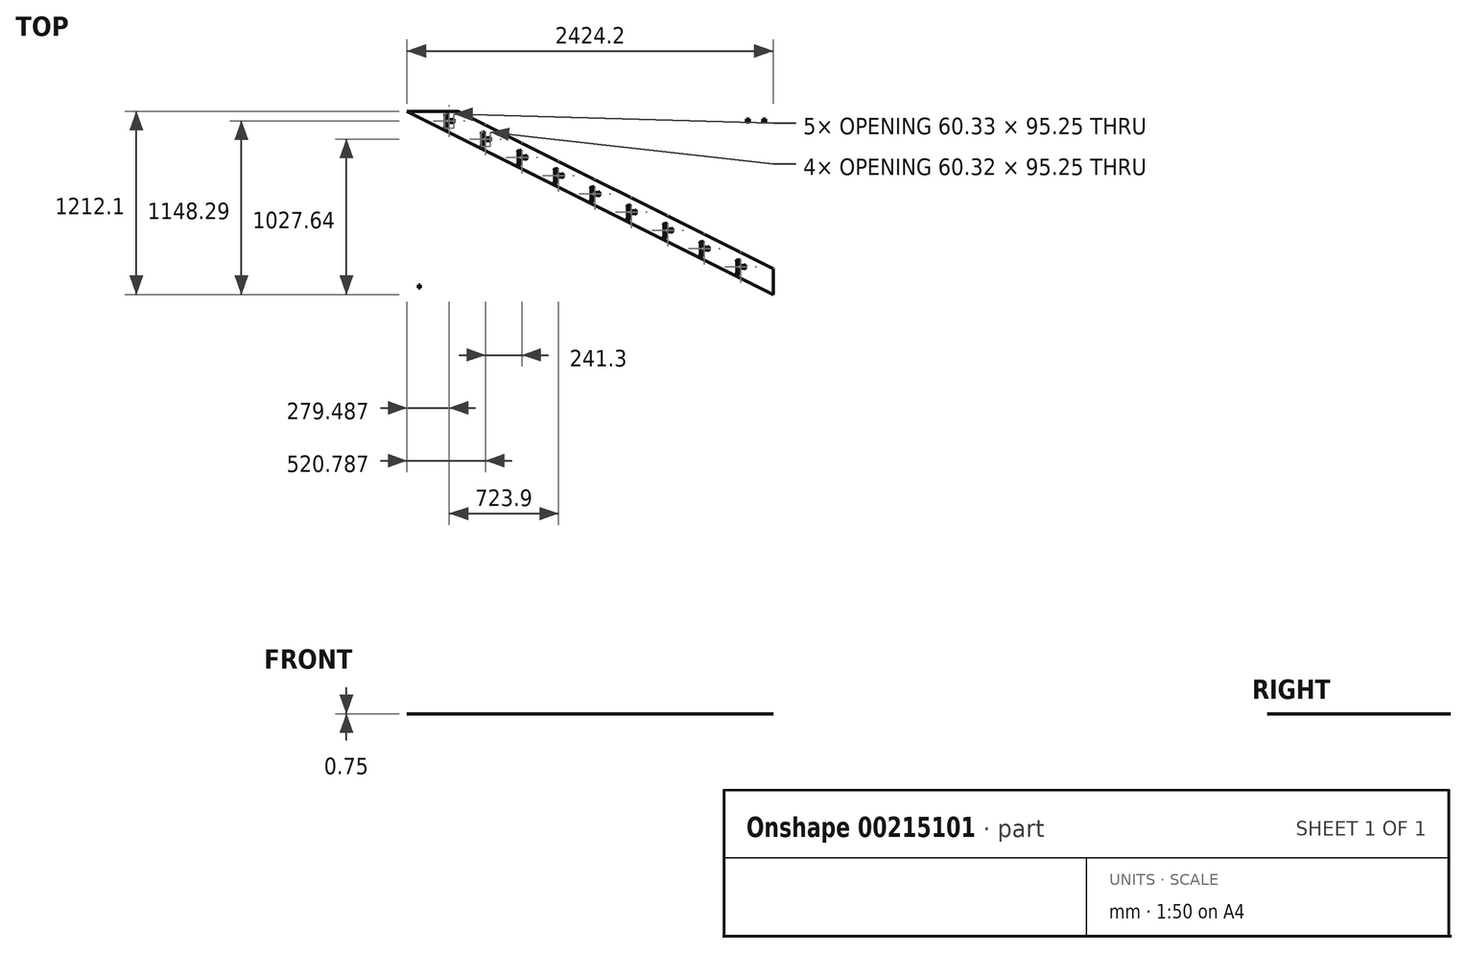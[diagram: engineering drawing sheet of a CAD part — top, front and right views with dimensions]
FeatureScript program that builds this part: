
annotation { "Feature Type Name" : "Feature", "Feature Type Description" : "" }
export const myFeature = defineFeature(function(context is Context, id is Id, definition is map)
    precondition{}
    {
        {
            assignVariable(context, id + "F0", {"name" : "Thickness", "anyValue" : 0.75});
        }
        {
            var Q0;
            Q0=qCreatedBy(makeId("Top.planeOp"),FACE);
            var sketch = newSketch(context, id + "F1", { "sketchPlane" : qUnion([Q0])});
            skLineSegment(sketch, "E0.0.0", {"start": v(-1223, -613.4) * mm, "end": v(1215.4, -613.4) * mm});
            skLineSegment(sketch, "E0.0.1", {"start": v(1215.4, -613.4) * mm, "end": v(1215.4, 605.8) * mm});
            skLineSegment(sketch, "E0.0.2", {"start": v(1215.4, 605.8) * mm, "end": v(-1223, 605.8) * mm});
            skLineSegment(sketch, "E0.0.3", {"start": v(-1223, 605.8) * mm, "end": v(-1223, -613.4) * mm});
            skLineSegment(sketch, "E1", {"start": v(-1223, 605.8) * mm, "end": v(1215.4, -613.4) * mm, "construction": true});
            skLineSegment(sketch, "E2.0", {"start": v(-1208.81, 605.8) * mm, "end": v(1215.4, -606.31) * mm});
            skLineSegment(sketch, "E3.0", {"start": v(-868.03, 605.8) * mm, "end": v(1215.4, -435.92) * mm});
            skLineSegment(sketch, "E4.1.0.0", {"start": v(974.1, -613.41) * mm, "end": v(974.1, 605.8) * mm, "construction": true});
            skLineSegment(sketch, "E4.2.0.0", {"start": v(732.8, -613.4) * mm, "end": v(732.8, 605.8) * mm, "construction": true});
            skLineSegment(sketch, "E4.direction1", {"start": v(1215.4, -613.4) * mm, "end": v(974.1, -613.4) * mm, "construction": true});
            skLineSegment(sketch, "E5.0.3.0", {"start": v(491.5, -613.4) * mm, "end": v(491.5, 605.8) * mm, "construction": true});
            skLineSegment(sketch, "E5.0.4.0", {"start": v(250.2, -613.4) * mm, "end": v(250.2, 605.8) * mm, "construction": true});
            skLineSegment(sketch, "E5.0.5.0", {"start": v(8.9, -613.4) * mm, "end": v(8.9, 605.8) * mm, "construction": true});
            skLineSegment(sketch, "E5.0.6.0", {"start": v(-232.4, -613.4) * mm, "end": v(-232.4, 605.8) * mm, "construction": true});
            skLineSegment(sketch, "E5.0.7.0", {"start": v(-473.7, -613.4) * mm, "end": v(-473.7, 605.8) * mm, "construction": true});
            skLineSegment(sketch, "E5.0.8.0", {"start": v(-715, -613.4) * mm, "end": v(-715, 605.8) * mm, "construction": true});
            skLineSegment(sketch, "E6.0.9.0", {"start": v(-956.3, -613.4) * mm, "end": v(-956.3, 605.8) * mm, "construction": true});
            skLineSegment(sketch, "E7.0.10.0", {"start": v(-1197.6, -613.4) * mm, "end": v(-1197.6, 605.8) * mm, "construction": true});
            skLineSegment(sketch, "E8.bottom", {"start": v(-956.31, 586.43) * mm, "end": v(-937.26, 586.43) * mm});
            skLineSegment(sketch, "E8.top", {"start": v(-956.31, 497.53) * mm, "end": v(-937.26, 497.53) * mm});
            skLineSegment(sketch, "E8.left", {"start": v(-956.3, 586.43) * mm, "end": v(-956.3, 497.53) * mm});
            skLineSegment(sketch, "E8.right", {"start": v(-937.26, 586.43) * mm, "end": v(-937.26, 497.53) * mm});
            skLineSegment(sketch, "E9.bottom", {"start": v(-715.01, 465.78) * mm, "end": v(-695.96, 465.78) * mm});
            skLineSegment(sketch, "E9.top", {"start": v(-715.01, 376.88) * mm, "end": v(-695.96, 376.88) * mm});
            skLineSegment(sketch, "E9.left", {"start": v(-715, 465.78) * mm, "end": v(-715, 376.88) * mm});
            skLineSegment(sketch, "E9.right", {"start": v(-695.96, 465.78) * mm, "end": v(-695.96, 376.88) * mm});
            skLineSegment(sketch, "E10.bottom", {"start": v(-473.71, 345.13) * mm, "end": v(-454.66, 345.13) * mm});
            skLineSegment(sketch, "E10.top", {"start": v(-473.7, 256.23) * mm, "end": v(-454.66, 256.23) * mm});
            skLineSegment(sketch, "E10.left", {"start": v(-473.7, 345.13) * mm, "end": v(-473.7, 256.23) * mm});
            skLineSegment(sketch, "E10.right", {"start": v(-454.66, 345.13) * mm, "end": v(-454.66, 256.23) * mm});
            skLineSegment(sketch, "E11.bottom", {"start": v(-232.4, 224.48) * mm, "end": v(-213.36, 224.48) * mm});
            skLineSegment(sketch, "E11.top", {"start": v(-232.4, 135.58) * mm, "end": v(-213.36, 135.58) * mm});
            skLineSegment(sketch, "E11.left", {"start": v(-232.4, 224.48) * mm, "end": v(-232.4, 135.58) * mm});
            skLineSegment(sketch, "E11.right", {"start": v(-213.36, 224.48) * mm, "end": v(-213.36, 135.58) * mm});
            skLineSegment(sketch, "E12.bottom", {"start": v(8.9, 103.83) * mm, "end": v(27.94, 103.83) * mm});
            skLineSegment(sketch, "E12.top", {"start": v(8.9, 14.93) * mm, "end": v(27.94, 14.93) * mm});
            skLineSegment(sketch, "E12.left", {"start": v(8.9, 103.83) * mm, "end": v(8.9, 14.93) * mm});
            skLineSegment(sketch, "E12.right", {"start": v(27.94, 103.83) * mm, "end": v(27.94, 14.93) * mm});
            skLineSegment(sketch, "E13.bottom", {"start": v(250.2, -16.82) * mm, "end": v(269.24, -16.82) * mm});
            skLineSegment(sketch, "E13.top", {"start": v(250.2, -105.72) * mm, "end": v(269.24, -105.72) * mm});
            skLineSegment(sketch, "E13.left", {"start": v(250.2, -16.82) * mm, "end": v(250.2, -105.72) * mm});
            skLineSegment(sketch, "E13.right", {"start": v(269.24, -16.82) * mm, "end": v(269.24, -105.72) * mm});
            skLineSegment(sketch, "E14.bottom", {"start": v(491.5, -137.47) * mm, "end": v(510.54, -137.47) * mm});
            skLineSegment(sketch, "E14.top", {"start": v(491.5, -226.37) * mm, "end": v(510.54, -226.37) * mm});
            skLineSegment(sketch, "E14.left", {"start": v(491.5, -137.47) * mm, "end": v(491.5, -226.37) * mm});
            skLineSegment(sketch, "E14.right", {"start": v(510.54, -137.47) * mm, "end": v(510.54, -226.37) * mm});
            skLineSegment(sketch, "E15.bottom", {"start": v(732.8, -258.12) * mm, "end": v(751.84, -258.12) * mm});
            skLineSegment(sketch, "E15.top", {"start": v(732.8, -347.02) * mm, "end": v(751.84, -347.02) * mm});
            skLineSegment(sketch, "E15.left", {"start": v(732.8, -258.12) * mm, "end": v(732.8, -347.02) * mm});
            skLineSegment(sketch, "E15.right", {"start": v(751.84, -258.12) * mm, "end": v(751.84, -347.02) * mm});
            skLineSegment(sketch, "E16.bottom", {"start": v(974.1, -378.77) * mm, "end": v(993.14, -378.77) * mm});
            skLineSegment(sketch, "E16.top", {"start": v(974.1, -467.67) * mm, "end": v(993.14, -467.67) * mm});
            skLineSegment(sketch, "E16.left", {"start": v(974.1, -378.77) * mm, "end": v(974.1, -467.67) * mm});
            skLineSegment(sketch, "E16.right", {"start": v(993.14, -378.77) * mm, "end": v(993.14, -467.67) * mm});
            skPoint(sketch, "E17", {"position": v(-715.01, 529.28) * mm});
            skPoint(sketch, "E18", {"position": v(-715, 358.89) * mm});
            skPoint(sketch, "E19", {"position": v(-473.71, 408.63) * mm});
            skPoint(sketch, "E20", {"position": v(-956.31, 649.93) * mm});
            skPoint(sketch, "E21", {"position": v(-232.41, 287.98) * mm});
            skPoint(sketch, "E22", {"position": v(8.89, 167.33) * mm});
            skPoint(sketch, "E23", {"position": v(250.19, 46.68) * mm});
            skPoint(sketch, "E24", {"position": v(491.49, -73.97) * mm});
            skPoint(sketch, "E25", {"position": v(732.8, -194.62) * mm});
            skPoint(sketch, "E26", {"position": v(974.1, -315.27) * mm});
            skLineSegment(sketch, "E27.top", {"start": v(-937.26, 532.45) * mm, "end": v(-899.16, 532.45) * mm});
            skLineSegment(sketch, "E27.left", {"start": v(-937.26, 551.5) * mm, "end": v(-937.26, 532.45) * mm});
            skLineSegment(sketch, "E27.right", {"start": v(-899.16, 551.5) * mm, "end": v(-899.16, 532.45) * mm});
            skLineSegment(sketch, "E28.bottom", {"start": v(-695.96, 430.85) * mm, "end": v(-657.86, 430.85) * mm});
            skLineSegment(sketch, "E28.top", {"start": v(-695.96, 411.8) * mm, "end": v(-657.86, 411.8) * mm});
            skLineSegment(sketch, "E28.left", {"start": v(-695.96, 430.85) * mm, "end": v(-695.96, 411.8) * mm});
            skLineSegment(sketch, "E28.right", {"start": v(-657.86, 430.85) * mm, "end": v(-657.86, 411.8) * mm});
            skLineSegment(sketch, "E29.bottom", {"start": v(-454.66, 310.2) * mm, "end": v(-416.56, 310.2) * mm});
            skLineSegment(sketch, "E29.top", {"start": v(-454.66, 291.15) * mm, "end": v(-416.56, 291.15) * mm});
            skLineSegment(sketch, "E29.left", {"start": v(-454.66, 310.2) * mm, "end": v(-454.66, 291.15) * mm});
            skLineSegment(sketch, "E29.right", {"start": v(-416.56, 310.2) * mm, "end": v(-416.56, 291.15) * mm});
            skLineSegment(sketch, "E30.bottom", {"start": v(-213.36, 189.55) * mm, "end": v(-175.26, 189.55) * mm});
            skLineSegment(sketch, "E30.top", {"start": v(-213.36, 170.5) * mm, "end": v(-175.26, 170.5) * mm});
            skLineSegment(sketch, "E30.left", {"start": v(-213.36, 189.55) * mm, "end": v(-213.36, 170.5) * mm});
            skLineSegment(sketch, "E30.right", {"start": v(-175.26, 189.55) * mm, "end": v(-175.26, 170.5) * mm});
            skLineSegment(sketch, "E31.bottom", {"start": v(27.94, 68.9) * mm, "end": v(66.04, 68.9) * mm});
            skLineSegment(sketch, "E31.top", {"start": v(27.94, 49.85) * mm, "end": v(66.04, 49.85) * mm});
            skLineSegment(sketch, "E31.left", {"start": v(27.94, 68.9) * mm, "end": v(27.94, 49.85) * mm});
            skLineSegment(sketch, "E31.right", {"start": v(66.04, 68.9) * mm, "end": v(66.04, 49.85) * mm});
            skPoint(sketch, "E32", {"position": v(-899.16, 541.98) * mm});
            skPoint(sketch, "E33", {"position": v(-657.86, 421.33) * mm});
            skPoint(sketch, "E34", {"position": v(-416.56, 300.68) * mm});
            skPoint(sketch, "E35", {"position": v(-175.26, 180.03) * mm});
            skPoint(sketch, "E36", {"position": v(66.04, 59.38) * mm});
            skLineSegment(sketch, "E37.bottom", {"start": v(269.24, -51.75) * mm, "end": v(307.34, -51.75) * mm});
            skLineSegment(sketch, "E37.top", {"start": v(269.24, -70.8) * mm, "end": v(307.34, -70.8) * mm});
            skLineSegment(sketch, "E37.left", {"start": v(269.24, -51.75) * mm, "end": v(269.24, -70.8) * mm});
            skLineSegment(sketch, "E37.right", {"start": v(307.34, -51.75) * mm, "end": v(307.34, -70.8) * mm});
            skPoint(sketch, "E38", {"position": v(307.34, -61.27) * mm});
            skLineSegment(sketch, "E39.bottom", {"start": v(510.54, -172.4) * mm, "end": v(548.64, -172.4) * mm});
            skLineSegment(sketch, "E39.top", {"start": v(510.54, -191.45) * mm, "end": v(548.64, -191.45) * mm});
            skLineSegment(sketch, "E39.left", {"start": v(510.54, -172.4) * mm, "end": v(510.54, -191.45) * mm});
            skLineSegment(sketch, "E39.right", {"start": v(548.64, -172.4) * mm, "end": v(548.64, -191.45) * mm});
            skPoint(sketch, "E40", {"position": v(548.64, -181.92) * mm});
            skLineSegment(sketch, "E41.bottom", {"start": v(751.84, -293.05) * mm, "end": v(789.94, -293.05) * mm});
            skLineSegment(sketch, "E41.top", {"start": v(751.84, -312.1) * mm, "end": v(789.94, -312.1) * mm});
            skLineSegment(sketch, "E41.left", {"start": v(751.84, -293.05) * mm, "end": v(751.84, -312.1) * mm});
            skLineSegment(sketch, "E41.right", {"start": v(789.94, -293.05) * mm, "end": v(789.94, -312.1) * mm});
            skLineSegment(sketch, "E42.bottom", {"start": v(993.14, -413.7) * mm, "end": v(1031.24, -413.7) * mm});
            skLineSegment(sketch, "E42.top", {"start": v(993.14, -432.75) * mm, "end": v(1031.24, -432.75) * mm});
            skLineSegment(sketch, "E42.left", {"start": v(993.14, -413.7) * mm, "end": v(993.14, -432.75) * mm});
            skLineSegment(sketch, "E42.right", {"start": v(1031.24, -413.7) * mm, "end": v(1031.24, -432.75) * mm});
            skPoint(sketch, "E43", {"position": v(1031.24, -423.22) * mm});
            skLineSegment(sketch, "E44.bottom", {"start": v(-1172.2, -562.6) * mm, "end": v(-1121.4, -562.6) * mm});
            skLineSegment(sketch, "E44.top", {"start": v(-1172.2, -54.6) * mm, "end": v(-1121.4, -54.6) * mm});
            skLineSegment(sketch, "E44.left", {"start": v(-1172.2, -562.6) * mm, "end": v(-1172.2, -54.6) * mm});
            skLineSegment(sketch, "E44.right", {"start": v(-1121.4, -562.6) * mm, "end": v(-1121.4, -54.61) * mm});
            skLineSegment(sketch, "E45.bottom", {"start": v(-1121.4, -54.6) * mm, "end": v(-1134.1, -54.6) * mm});
            skLineSegment(sketch, "E45.top", {"start": v(-1121.4, -73.66) * mm, "end": v(-1134.1, -73.66) * mm});
            skLineSegment(sketch, "E45.left", {"start": v(-1121.4, -54.61) * mm, "end": v(-1121.4, -73.66) * mm});
            skLineSegment(sketch, "E45.right", {"start": v(-1134.1, -54.61) * mm, "end": v(-1134.1, -73.66) * mm});
            skLineSegment(sketch, "E46.bottom", {"start": v(-1121.4, -562.6) * mm, "end": v(-1134.1, -562.6) * mm});
            skLineSegment(sketch, "E46.top", {"start": v(-1121.4, -543.56) * mm, "end": v(-1134.1, -543.56) * mm});
            skLineSegment(sketch, "E46.left", {"start": v(-1121.4, -562.6) * mm, "end": v(-1121.4, -543.56) * mm});
            skLineSegment(sketch, "E46.right", {"start": v(-1134.1, -562.61) * mm, "end": v(-1134.1, -543.56) * mm});
            skLineSegment(sketch, "E47.1.0.0", {"start": v(-1062.99, -73.66) * mm, "end": v(-1075.69, -73.66) * mm});
            skLineSegment(sketch, "E47.1.0.1", {"start": v(-1075.69, -54.61) * mm, "end": v(-1075.69, -73.66) * mm});
            skLineSegment(sketch, "E47.1.0.2", {"start": v(-1075.69, -562.61) * mm, "end": v(-1075.69, -543.56) * mm});
            skLineSegment(sketch, "E47.1.0.3", {"start": v(-1113.8, -562.6) * mm, "end": v(-1062.99, -562.6) * mm});
            skLineSegment(sketch, "E47.1.0.4", {"start": v(-1113.79, -54.6) * mm, "end": v(-1062.99, -54.6) * mm});
            skLineSegment(sketch, "E47.1.0.5", {"start": v(-1113.8, -562.6) * mm, "end": v(-1113.79, -54.6) * mm});
            skLineSegment(sketch, "E47.1.0.6", {"start": v(-1062.99, -562.6) * mm, "end": v(-1062.99, -54.61) * mm});
            skLineSegment(sketch, "E47.1.0.7", {"start": v(-1062.99, -54.6) * mm, "end": v(-1075.69, -54.6) * mm});
            skLineSegment(sketch, "E47.1.0.8", {"start": v(-1062.99, -54.61) * mm, "end": v(-1062.99, -73.66) * mm});
            skLineSegment(sketch, "E47.1.0.9", {"start": v(-1062.99, -562.6) * mm, "end": v(-1062.99, -543.56) * mm});
            skLineSegment(sketch, "E47.1.0.10", {"start": v(-1062.99, -562.6) * mm, "end": v(-1075.69, -562.6) * mm});
            skLineSegment(sketch, "E47.1.0.11", {"start": v(-1062.99, -543.56) * mm, "end": v(-1075.7, -543.56) * mm});
            skLineSegment(sketch, "E47.2.0.0", {"start": v(-1004.57, -73.66) * mm, "end": v(-1017.27, -73.66) * mm});
            skLineSegment(sketch, "E47.2.0.1", {"start": v(-1017.27, -54.61) * mm, "end": v(-1017.27, -73.66) * mm});
            skLineSegment(sketch, "E47.2.0.2", {"start": v(-1017.27, -562.61) * mm, "end": v(-1017.27, -543.56) * mm});
            skLineSegment(sketch, "E47.2.0.3", {"start": v(-1055.37, -562.6) * mm, "end": v(-1004.57, -562.6) * mm});
            skLineSegment(sketch, "E47.2.0.4", {"start": v(-1055.37, -54.6) * mm, "end": v(-1004.57, -54.6) * mm});
            skLineSegment(sketch, "E47.2.0.5", {"start": v(-1055.37, -562.6) * mm, "end": v(-1055.37, -54.6) * mm});
            skLineSegment(sketch, "E47.2.0.6", {"start": v(-1004.57, -562.6) * mm, "end": v(-1004.57, -54.61) * mm});
            skLineSegment(sketch, "E47.2.0.7", {"start": v(-1004.57, -54.6) * mm, "end": v(-1017.27, -54.6) * mm});
            skLineSegment(sketch, "E47.2.0.8", {"start": v(-1004.57, -54.61) * mm, "end": v(-1004.57, -73.66) * mm});
            skLineSegment(sketch, "E47.2.0.9", {"start": v(-1004.57, -562.6) * mm, "end": v(-1004.57, -543.56) * mm});
            skLineSegment(sketch, "E47.2.0.10", {"start": v(-1004.57, -562.6) * mm, "end": v(-1017.27, -562.6) * mm});
            skLineSegment(sketch, "E47.2.0.11", {"start": v(-1004.57, -543.56) * mm, "end": v(-1017.27, -543.56) * mm});
            skLineSegment(sketch, "E47.3.0.0", {"start": v(-946.15, -73.66) * mm, "end": v(-958.85, -73.66) * mm});
            skLineSegment(sketch, "E47.3.0.1", {"start": v(-958.85, -54.61) * mm, "end": v(-958.85, -73.66) * mm});
            skLineSegment(sketch, "E47.3.0.2", {"start": v(-958.85, -562.61) * mm, "end": v(-958.85, -543.56) * mm});
            skLineSegment(sketch, "E47.3.0.3", {"start": v(-996.95, -562.6) * mm, "end": v(-946.15, -562.6) * mm});
            skLineSegment(sketch, "E47.3.0.4", {"start": v(-996.95, -54.6) * mm, "end": v(-946.15, -54.6) * mm});
            skLineSegment(sketch, "E47.3.0.5", {"start": v(-996.95, -562.6) * mm, "end": v(-996.95, -54.6) * mm});
            skLineSegment(sketch, "E47.3.0.6", {"start": v(-946.15, -562.6) * mm, "end": v(-946.15, -54.61) * mm});
            skLineSegment(sketch, "E47.3.0.7", {"start": v(-946.15, -54.6) * mm, "end": v(-958.85, -54.6) * mm});
            skLineSegment(sketch, "E47.3.0.8", {"start": v(-946.15, -54.61) * mm, "end": v(-946.15, -73.66) * mm});
            skLineSegment(sketch, "E47.3.0.9", {"start": v(-946.15, -562.6) * mm, "end": v(-946.15, -543.56) * mm});
            skLineSegment(sketch, "E47.3.0.10", {"start": v(-946.15, -562.6) * mm, "end": v(-958.85, -562.6) * mm});
            skLineSegment(sketch, "E47.3.0.11", {"start": v(-946.15, -543.56) * mm, "end": v(-958.85, -543.56) * mm});
            skLineSegment(sketch, "E47.4.0.0", {"start": v(-887.73, -73.66) * mm, "end": v(-900.43, -73.66) * mm});
            skLineSegment(sketch, "E47.4.0.1", {"start": v(-900.43, -54.61) * mm, "end": v(-900.43, -73.66) * mm});
            skLineSegment(sketch, "E47.4.0.2", {"start": v(-900.43, -562.61) * mm, "end": v(-900.43, -543.56) * mm});
            skLineSegment(sketch, "E47.4.0.3", {"start": v(-938.53, -562.6) * mm, "end": v(-887.73, -562.6) * mm});
            skLineSegment(sketch, "E47.4.0.4", {"start": v(-938.53, -54.6) * mm, "end": v(-887.73, -54.6) * mm});
            skLineSegment(sketch, "E47.4.0.5", {"start": v(-938.53, -562.6) * mm, "end": v(-938.53, -54.6) * mm});
            skLineSegment(sketch, "E47.4.0.6", {"start": v(-887.73, -562.6) * mm, "end": v(-887.73, -54.61) * mm});
            skLineSegment(sketch, "E47.4.0.7", {"start": v(-887.73, -54.6) * mm, "end": v(-900.43, -54.6) * mm});
            skLineSegment(sketch, "E47.4.0.8", {"start": v(-887.73, -54.61) * mm, "end": v(-887.73, -73.66) * mm});
            skLineSegment(sketch, "E47.4.0.9", {"start": v(-887.73, -562.6) * mm, "end": v(-887.73, -543.56) * mm});
            skLineSegment(sketch, "E47.4.0.10", {"start": v(-887.73, -562.6) * mm, "end": v(-900.43, -562.6) * mm});
            skLineSegment(sketch, "E47.4.0.11", {"start": v(-887.73, -543.56) * mm, "end": v(-900.43, -543.56) * mm});
            skLineSegment(sketch, "E47.5.0.0", {"start": v(-829.31, -73.66) * mm, "end": v(-842.01, -73.66) * mm});
            skLineSegment(sketch, "E47.5.0.1", {"start": v(-842.01, -54.61) * mm, "end": v(-842.01, -73.66) * mm});
            skLineSegment(sketch, "E47.5.0.2", {"start": v(-842.01, -562.61) * mm, "end": v(-842.01, -543.56) * mm});
            skLineSegment(sketch, "E47.5.0.3", {"start": v(-880.11, -562.6) * mm, "end": v(-829.31, -562.6) * mm});
            skLineSegment(sketch, "E47.5.0.4", {"start": v(-880.11, -54.6) * mm, "end": v(-829.31, -54.6) * mm});
            skLineSegment(sketch, "E47.5.0.5", {"start": v(-880.11, -562.6) * mm, "end": v(-880.11, -54.6) * mm});
            skLineSegment(sketch, "E47.5.0.6", {"start": v(-829.31, -562.6) * mm, "end": v(-829.31, -54.61) * mm});
            skLineSegment(sketch, "E47.5.0.7", {"start": v(-829.31, -54.6) * mm, "end": v(-842.01, -54.6) * mm});
            skLineSegment(sketch, "E47.5.0.8", {"start": v(-829.31, -54.61) * mm, "end": v(-829.31, -73.66) * mm});
            skLineSegment(sketch, "E47.5.0.9", {"start": v(-829.31, -562.6) * mm, "end": v(-829.31, -543.56) * mm});
            skLineSegment(sketch, "E47.5.0.10", {"start": v(-829.31, -562.6) * mm, "end": v(-842.01, -562.6) * mm});
            skLineSegment(sketch, "E47.5.0.11", {"start": v(-829.31, -543.56) * mm, "end": v(-842.01, -543.56) * mm});
            skLineSegment(sketch, "E47.6.0.0", {"start": v(-770.9, -73.66) * mm, "end": v(-783.6, -73.66) * mm});
            skLineSegment(sketch, "E47.6.0.1", {"start": v(-783.6, -54.61) * mm, "end": v(-783.6, -73.66) * mm});
            skLineSegment(sketch, "E47.6.0.2", {"start": v(-783.6, -562.61) * mm, "end": v(-783.6, -543.56) * mm});
            skLineSegment(sketch, "E47.6.0.3", {"start": v(-821.7, -562.6) * mm, "end": v(-770.9, -562.6) * mm});
            skLineSegment(sketch, "E47.6.0.4", {"start": v(-821.7, -54.6) * mm, "end": v(-770.9, -54.6) * mm});
            skLineSegment(sketch, "E47.6.0.5", {"start": v(-821.7, -562.6) * mm, "end": v(-821.7, -54.6) * mm});
            skLineSegment(sketch, "E47.6.0.6", {"start": v(-770.9, -562.6) * mm, "end": v(-770.9, -54.61) * mm});
            skLineSegment(sketch, "E47.6.0.7", {"start": v(-770.9, -54.6) * mm, "end": v(-783.6, -54.6) * mm});
            skLineSegment(sketch, "E47.6.0.8", {"start": v(-770.9, -54.61) * mm, "end": v(-770.9, -73.66) * mm});
            skLineSegment(sketch, "E47.6.0.9", {"start": v(-770.9, -562.6) * mm, "end": v(-770.9, -543.56) * mm});
            skLineSegment(sketch, "E47.6.0.10", {"start": v(-770.9, -562.6) * mm, "end": v(-783.6, -562.6) * mm});
            skLineSegment(sketch, "E47.6.0.11", {"start": v(-770.9, -543.56) * mm, "end": v(-783.6, -543.56) * mm});
            skLineSegment(sketch, "E47.7.0.0", {"start": v(-712.47, -73.66) * mm, "end": v(-725.17, -73.66) * mm});
            skLineSegment(sketch, "E47.7.0.1", {"start": v(-725.17, -54.61) * mm, "end": v(-725.17, -73.66) * mm});
            skLineSegment(sketch, "E47.7.0.2", {"start": v(-725.17, -562.61) * mm, "end": v(-725.17, -543.56) * mm});
            skLineSegment(sketch, "E47.7.0.3", {"start": v(-763.27, -562.6) * mm, "end": v(-712.47, -562.6) * mm});
            skLineSegment(sketch, "E47.7.0.4", {"start": v(-763.27, -54.6) * mm, "end": v(-712.47, -54.6) * mm});
            skLineSegment(sketch, "E47.7.0.5", {"start": v(-763.27, -562.6) * mm, "end": v(-763.27, -54.6) * mm});
            skLineSegment(sketch, "E47.7.0.6", {"start": v(-712.47, -562.6) * mm, "end": v(-712.47, -54.61) * mm});
            skLineSegment(sketch, "E47.7.0.7", {"start": v(-712.47, -54.6) * mm, "end": v(-725.17, -54.6) * mm});
            skLineSegment(sketch, "E47.7.0.8", {"start": v(-712.47, -54.61) * mm, "end": v(-712.47, -73.66) * mm});
            skLineSegment(sketch, "E47.7.0.9", {"start": v(-712.47, -562.6) * mm, "end": v(-712.47, -543.56) * mm});
            skLineSegment(sketch, "E47.7.0.10", {"start": v(-712.47, -562.6) * mm, "end": v(-725.17, -562.6) * mm});
            skLineSegment(sketch, "E47.7.0.11", {"start": v(-712.47, -543.56) * mm, "end": v(-725.17, -543.56) * mm});
            skLineSegment(sketch, "E47.8.0.0", {"start": v(-654.05, -73.66) * mm, "end": v(-666.75, -73.66) * mm});
            skLineSegment(sketch, "E47.8.0.1", {"start": v(-666.75, -54.61) * mm, "end": v(-666.75, -73.66) * mm});
            skLineSegment(sketch, "E47.8.0.2", {"start": v(-666.75, -562.61) * mm, "end": v(-666.75, -543.56) * mm});
            skLineSegment(sketch, "E47.8.0.3", {"start": v(-704.85, -562.6) * mm, "end": v(-654.05, -562.6) * mm});
            skLineSegment(sketch, "E47.8.0.4", {"start": v(-704.85, -54.6) * mm, "end": v(-654.05, -54.6) * mm});
            skLineSegment(sketch, "E47.8.0.5", {"start": v(-704.85, -562.6) * mm, "end": v(-704.85, -54.6) * mm});
            skLineSegment(sketch, "E47.8.0.6", {"start": v(-654.05, -562.6) * mm, "end": v(-654.05, -54.61) * mm});
            skLineSegment(sketch, "E47.8.0.7", {"start": v(-654.05, -54.6) * mm, "end": v(-666.75, -54.6) * mm});
            skLineSegment(sketch, "E47.8.0.8", {"start": v(-654.05, -54.61) * mm, "end": v(-654.05, -73.66) * mm});
            skLineSegment(sketch, "E47.8.0.9", {"start": v(-654.05, -562.6) * mm, "end": v(-654.05, -543.56) * mm});
            skLineSegment(sketch, "E47.8.0.10", {"start": v(-654.05, -562.6) * mm, "end": v(-666.75, -562.6) * mm});
            skLineSegment(sketch, "E47.8.0.11", {"start": v(-654.05, -543.56) * mm, "end": v(-666.75, -543.56) * mm});
            skLineSegment(sketch, "E47.9.0.0", {"start": v(-595.63, -73.66) * mm, "end": v(-608.33, -73.66) * mm});
            skLineSegment(sketch, "E47.9.0.1", {"start": v(-608.33, -54.61) * mm, "end": v(-608.33, -73.66) * mm});
            skLineSegment(sketch, "E47.9.0.2", {"start": v(-608.33, -562.61) * mm, "end": v(-608.33, -543.56) * mm});
            skLineSegment(sketch, "E47.9.0.3", {"start": v(-646.43, -562.6) * mm, "end": v(-595.63, -562.6) * mm});
            skLineSegment(sketch, "E47.9.0.4", {"start": v(-646.43, -54.6) * mm, "end": v(-595.63, -54.6) * mm});
            skLineSegment(sketch, "E47.9.0.5", {"start": v(-646.43, -562.6) * mm, "end": v(-646.43, -54.6) * mm});
            skLineSegment(sketch, "E47.9.0.6", {"start": v(-595.63, -562.6) * mm, "end": v(-595.63, -54.61) * mm});
            skLineSegment(sketch, "E47.9.0.7", {"start": v(-595.63, -54.6) * mm, "end": v(-608.33, -54.6) * mm});
            skLineSegment(sketch, "E47.9.0.8", {"start": v(-595.63, -54.61) * mm, "end": v(-595.63, -73.66) * mm});
            skLineSegment(sketch, "E47.9.0.9", {"start": v(-595.63, -562.6) * mm, "end": v(-595.63, -543.56) * mm});
            skLineSegment(sketch, "E47.9.0.10", {"start": v(-595.63, -562.6) * mm, "end": v(-608.33, -562.6) * mm});
            skLineSegment(sketch, "E47.9.0.11", {"start": v(-595.63, -543.56) * mm, "end": v(-608.33, -543.56) * mm});
            skLineSegment(sketch, "E47.direction1", {"start": v(-1172.2, -562.6) * mm, "end": v(-1113.8, -562.6) * mm, "construction": true});
            skLineSegment(sketch, "E48", {"start": v(-937.26, 551.5) * mm, "end": v(-899.16, 551.5) * mm});
            skLineSegment(sketch, "E49.bottom", {"start": v(1037.6, 555) * mm, "end": v(1164.6, 555) * mm});
            skLineSegment(sketch, "E49.top", {"start": v(1037.6, 47) * mm, "end": v(1164.6, 47) * mm});
            skLineSegment(sketch, "E49.left", {"start": v(1037.6, 555) * mm, "end": v(1037.6, 47) * mm});
            skLineSegment(sketch, "E49.right", {"start": v(1164.6, 555) * mm, "end": v(1164.6, 47) * mm});
            skLineSegment(sketch, "E50.bottom", {"start": v(1037.6, 555) * mm, "end": v(1056.64, 555) * mm});
            skLineSegment(sketch, "E50.top", {"start": v(1037.6, 535.94) * mm, "end": v(1056.64, 535.94) * mm});
            skLineSegment(sketch, "E50.left", {"start": v(1037.6, 555) * mm, "end": v(1037.6, 535.94) * mm});
            skLineSegment(sketch, "E50.right", {"start": v(1056.64, 555) * mm, "end": v(1056.64, 535.94) * mm});
            skLineSegment(sketch, "E51.bottom", {"start": v(1164.6, 555) * mm, "end": v(1145.54, 555) * mm});
            skLineSegment(sketch, "E51.top", {"start": v(1164.59, 535.94) * mm, "end": v(1145.54, 535.94) * mm});
            skLineSegment(sketch, "E51.left", {"start": v(1164.6, 555) * mm, "end": v(1164.6, 535.94) * mm});
            skLineSegment(sketch, "E51.right", {"start": v(1145.54, 555) * mm, "end": v(1145.54, 535.94) * mm});
            skLineSegment(sketch, "E52.bottom", {"start": v(1037.6, 47) * mm, "end": v(1056.64, 47) * mm});
            skLineSegment(sketch, "E52.top", {"start": v(1037.6, 66.04) * mm, "end": v(1056.64, 66.04) * mm});
            skLineSegment(sketch, "E52.left", {"start": v(1037.6, 47) * mm, "end": v(1037.6, 66.04) * mm});
            skLineSegment(sketch, "E52.right", {"start": v(1056.64, 47) * mm, "end": v(1056.64, 66.04) * mm});
            skLineSegment(sketch, "E53.bottom", {"start": v(1164.6, 47) * mm, "end": v(1145.54, 47) * mm});
            skLineSegment(sketch, "E53.top", {"start": v(1164.6, 66.04) * mm, "end": v(1145.54, 66.04) * mm});
            skLineSegment(sketch, "E53.left", {"start": v(1164.6, 47) * mm, "end": v(1164.6, 66.04) * mm});
            skLineSegment(sketch, "E53.right", {"start": v(1145.54, 47) * mm, "end": v(1145.54, 66.04) * mm});
            skPoint(sketch, "E54", {"position": v(789.94, -302.57) * mm});
            skArc(sketch, "E55", {"start": v(-1134.1, -73.66) * mm, "mid": v(-1130.93, -76.84) * mm, "end": v(-1127.76, -73.66) * mm});
            skArc(sketch, "E56", {"start": v(-1127.76, -543.56) * mm, "mid": v(-1130.93, -540.39) * mm, "end": v(-1134.1, -543.56) * mm});
            skArc(sketch, "E57", {"start": v(1056.64, 66.04) * mm, "mid": v(1053.47, 69.22) * mm, "end": v(1050.3, 66.04) * mm});
            skArc(sketch, "E58", {"start": v(1151.89, 66.04) * mm, "mid": v(1148.71, 69.22) * mm, "end": v(1145.54, 66.04) * mm});
            skArc(sketch, "E59", {"start": v(1050.3, 535.94) * mm, "mid": v(1053.47, 532.77) * mm, "end": v(1056.64, 535.94) * mm});
            skArc(sketch, "E60", {"start": v(1145.54, 535.94) * mm, "mid": v(1148.71, 532.77) * mm, "end": v(1151.89, 535.94) * mm});
            skArc(sketch, "E61", {"start": v(-899.16, 551.5) * mm, "mid": v(-902.34, 554.68) * mm, "end": v(-905.51, 551.5) * mm});
            skArc(sketch, "E62", {"start": v(-905.51, 532.45) * mm, "mid": v(-902.34, 529.28) * mm, "end": v(-899.16, 532.45) * mm});
            skArc(sketch, "E63", {"start": v(-937.26, 586.43) * mm, "mid": v(-940.44, 589.6) * mm, "end": v(-943.61, 586.43) * mm});
            skArc(sketch, "E64", {"start": v(-943.61, 497.53) * mm, "mid": v(-940.44, 494.35) * mm, "end": v(-937.26, 497.53) * mm});
            skArc(sketch, "E65", {"start": v(-956.31, 503.88) * mm, "mid": v(-959.49, 500.7) * mm, "end": v(-956.31, 497.53) * mm});
            skArc(sketch, "E66", {"start": v(-956.31, 586.43) * mm, "mid": v(-959.49, 583.25) * mm, "end": v(-956.31, 580.08) * mm});
            skArc(sketch, "E67", {"start": v(-657.86, 430.85) * mm, "mid": v(-661.04, 434.03) * mm, "end": v(-664.21, 430.85) * mm});
            skArc(sketch, "E68", {"start": v(-664.21, 411.8) * mm, "mid": v(-661.04, 408.63) * mm, "end": v(-657.86, 411.8) * mm});
            skArc(sketch, "E69", {"start": v(-695.96, 465.78) * mm, "mid": v(-699.14, 468.95) * mm, "end": v(-702.31, 465.78) * mm});
            skArc(sketch, "E70", {"start": v(-715.01, 465.78) * mm, "mid": v(-718.19, 462.6) * mm, "end": v(-715, 459.43) * mm});
            skArc(sketch, "E71", {"start": v(-702.31, 376.88) * mm, "mid": v(-699.14, 373.7) * mm, "end": v(-695.96, 376.88) * mm});
            skArc(sketch, "E72", {"start": v(-715.01, 383.23) * mm, "mid": v(-718.19, 380.05) * mm, "end": v(-715.01, 376.88) * mm});
            skArc(sketch, "E73", {"start": v(-416.56, 310.2) * mm, "mid": v(-419.73, 313.38) * mm, "end": v(-422.9, 310.2) * mm});
            skArc(sketch, "E74", {"start": v(-422.9, 291.15) * mm, "mid": v(-419.73, 287.98) * mm, "end": v(-416.56, 291.15) * mm});
            skArc(sketch, "E75", {"start": v(-454.66, 345.13) * mm, "mid": v(-457.83, 348.3) * mm, "end": v(-461, 345.13) * mm});
            skArc(sketch, "E76", {"start": v(-461, 256.23) * mm, "mid": v(-457.83, 253.05) * mm, "end": v(-454.66, 256.23) * mm});
            skArc(sketch, "E77", {"start": v(-473.71, 345.13) * mm, "mid": v(-476.88, 341.95) * mm, "end": v(-473.71, 338.78) * mm});
            skArc(sketch, "E78", {"start": v(-473.71, 262.58) * mm, "mid": v(-476.88, 259.4) * mm, "end": v(-473.7, 256.23) * mm});
            skArc(sketch, "E79", {"start": v(-175.26, 189.55) * mm, "mid": v(-178.43, 192.73) * mm, "end": v(-181.6, 189.55) * mm});
            skArc(sketch, "E80", {"start": v(-213.36, 224.48) * mm, "mid": v(-216.53, 227.65) * mm, "end": v(-219.7, 224.48) * mm});
            skArc(sketch, "E81", {"start": v(-219.7, 135.58) * mm, "mid": v(-216.53, 132.4) * mm, "end": v(-213.36, 135.58) * mm});
            skArc(sketch, "E82", {"start": v(-232.4, 224.48) * mm, "mid": v(-235.58, 221.3) * mm, "end": v(-232.4, 218.13) * mm});
            skArc(sketch, "E83", {"start": v(-232.4, 141.93) * mm, "mid": v(-235.58, 138.75) * mm, "end": v(-232.4, 135.58) * mm});
            skArc(sketch, "E84", {"start": v(66.04, 68.9) * mm, "mid": v(62.87, 72.08) * mm, "end": v(59.7, 68.9) * mm});
            skArc(sketch, "E85", {"start": v(59.7, 49.85) * mm, "mid": v(62.87, 46.68) * mm, "end": v(66.04, 49.85) * mm});
            skArc(sketch, "E86", {"start": v(27.94, 103.83) * mm, "mid": v(24.77, 107) * mm, "end": v(21.6, 103.83) * mm});
            skArc(sketch, "E87", {"start": v(21.6, 14.93) * mm, "mid": v(24.77, 11.75) * mm, "end": v(27.94, 14.93) * mm});
            skArc(sketch, "E88", {"start": v(8.9, 103.83) * mm, "mid": v(5.72, 100.65) * mm, "end": v(8.9, 97.48) * mm});
            skArc(sketch, "E89", {"start": v(8.9, 21.28) * mm, "mid": v(5.72, 18.1) * mm, "end": v(8.9, 14.93) * mm});
            skArc(sketch, "E90", {"start": v(301, -70.8) * mm, "mid": v(304.17, -73.97) * mm, "end": v(307.34, -70.8) * mm});
            skArc(sketch, "E91", {"start": v(307.34, -51.75) * mm, "mid": v(304.17, -48.57) * mm, "end": v(301, -51.75) * mm});
            skArc(sketch, "E92", {"start": v(269.24, -16.82) * mm, "mid": v(266.07, -13.65) * mm, "end": v(262.9, -16.82) * mm});
            skArc(sketch, "E93", {"start": v(262.9, -105.72) * mm, "mid": v(266.07, -108.9) * mm, "end": v(269.24, -105.72) * mm});
            skArc(sketch, "E94", {"start": v(250.2, -16.82) * mm, "mid": v(247.02, -20) * mm, "end": v(250.2, -23.17) * mm});
            skArc(sketch, "E95", {"start": v(250.2, -99.37) * mm, "mid": v(247.02, -102.55) * mm, "end": v(250.2, -105.72) * mm});
            skArc(sketch, "E96", {"start": v(548.64, -172.4) * mm, "mid": v(545.47, -169.22) * mm, "end": v(542.3, -172.4) * mm});
            skArc(sketch, "E97", {"start": v(542.3, -191.45) * mm, "mid": v(545.47, -194.62) * mm, "end": v(548.64, -191.45) * mm});
            skArc(sketch, "E98", {"start": v(510.54, -137.47) * mm, "mid": v(507.37, -134.3) * mm, "end": v(504.2, -137.47) * mm});
            skArc(sketch, "E99", {"start": v(504.2, -226.37) * mm, "mid": v(507.37, -229.55) * mm, "end": v(510.54, -226.37) * mm});
            skArc(sketch, "E100", {"start": v(491.5, -137.47) * mm, "mid": v(488.32, -140.65) * mm, "end": v(491.5, -143.82) * mm});
            skArc(sketch, "E101", {"start": v(491.5, -220.02) * mm, "mid": v(488.32, -223.2) * mm, "end": v(491.5, -226.37) * mm});
            skArc(sketch, "E102", {"start": v(789.94, -293.05) * mm, "mid": v(786.77, -289.87) * mm, "end": v(783.6, -293.05) * mm});
            skArc(sketch, "E103", {"start": v(783.6, -312.1) * mm, "mid": v(786.77, -315.27) * mm, "end": v(789.94, -312.1) * mm});
            skArc(sketch, "E104", {"start": v(751.84, -258.12) * mm, "mid": v(748.67, -254.95) * mm, "end": v(745.5, -258.12) * mm});
            skArc(sketch, "E105", {"start": v(745.5, -347.02) * mm, "mid": v(748.67, -350.2) * mm, "end": v(751.84, -347.02) * mm});
            skArc(sketch, "E106", {"start": v(732.8, -258.12) * mm, "mid": v(729.62, -261.3) * mm, "end": v(732.8, -264.47) * mm});
            skArc(sketch, "E107", {"start": v(732.8, -340.67) * mm, "mid": v(729.62, -343.85) * mm, "end": v(732.8, -347.02) * mm});
            skArc(sketch, "E108", {"start": v(1031.24, -413.7) * mm, "mid": v(1028.07, -410.52) * mm, "end": v(1024.9, -413.7) * mm});
            skArc(sketch, "E109", {"start": v(1024.9, -432.75) * mm, "mid": v(1028.07, -435.92) * mm, "end": v(1031.24, -432.75) * mm});
            skArc(sketch, "E110", {"start": v(986.8, -467.67) * mm, "mid": v(989.97, -470.85) * mm, "end": v(993.14, -467.67) * mm});
            skArc(sketch, "E111", {"start": v(993.14, -378.77) * mm, "mid": v(989.97, -375.6) * mm, "end": v(986.8, -378.77) * mm});
            skArc(sketch, "E112", {"start": v(974.1, -378.77) * mm, "mid": v(970.92, -381.95) * mm, "end": v(974.1, -385.12) * mm});
            skArc(sketch, "E113", {"start": v(974.1, -461.32) * mm, "mid": v(970.92, -464.5) * mm, "end": v(974.1, -467.67) * mm});
            skArc(sketch, "E114", {"start": v(-181.6, 170.5) * mm, "mid": v(-178.43, 167.33) * mm, "end": v(-175.26, 170.5) * mm});
            skSolve(sketch);
        }
        {
            var Q0;
            {var subQ18=sQuery(id+"F1.wireOp",EDGE,"E2.0");Q0=makeQuery(id+"F1.imprint","IMPRINT",FACE,{"disambiguationData":[TD([[makeQuery(id+"F1.imprint","IMPRINT",EDGE,{"derivedFrom":subQ18}),1.0]])]});}
            var Q1;
            Q1=makeQuery(id+"F1.imprint","IMPRINT",FACE,{"disambiguationData":[TD([[makeQuery(id+"F1.imprint","IMPRINT",EDGE,{"derivedFrom":sQuery(id+"F1.wireOp",EDGE,"77cf4bd5-51a6-426d-9851-ebf729fd20c2")}),1.0]])]});
            var Q2;
            Q2=makeQuery(id+"F1.imprint","IMPRINT",FACE,{"disambiguationData":[TD([[makeQuery(id+"F1.imprint","IMPRINT",EDGE,{"derivedFrom":sQuery(id+"F1.wireOp",EDGE,"E44.bottom")}),1.0]])]});
            var Q3;
            Q3=makeQuery(id+"F1.imprint","IMPRINT",FACE,{"disambiguationData":[TD([[makeQuery(id+"F1.imprint","IMPRINT",EDGE,{"derivedFrom":sQuery(id+"F1.wireOp",EDGE,"E49.bottom")}),-1.0]])]});
            extrude(context, id + "F2", {"entities" : qUnion([Q0, Q1, Q2, Q3]), "depth" : (getVariable(context, 'Thickness')) * mm});
        }
    });
